# Revit family: GR_Решетка_РАГ-НГ-H_Вытяжка_R21
name_source: partatom
category: Воздухораспределители
units: mm (PartAtom-declared; Revit-internal decimal feet)

## family parameters
Всегда вертикально = Да
Заголовок OmniClass = Diffusers, Registers, and Grilles
На основе рабочей плоскости = Нет
Номер OmniClass = 23.75.70.21.27.11
Общий = Нет
При загрузке вырезать с полостями = Да
Размер круглого соединителя = Использовать диаметр
Тип детали = Нормальный
Точка принадлежности помещению = Нет

## types (2) — shared parameters
ADSK_URL страницы изделия = https://grilles.ru
ADSK_Автор = THE GRILLES
ADSK_Версия Revit = 2021
ADSK_Версия семейства = v1
ADSK_Единица измерения = шт.
ADSK_Завод-изготовитель = ООО "ВЕНТРЕШЕТКИКОМ"
ADSK_Код изделия = 002057
ADSK_Количество = 1
ADSK_Наименование = Решетка нерегулируемая вытяжная РАГ-НГ-Н
GR_Материал решетки = Сталь, RAL 9016M, белый
URL = https://grilles.ru
Изготовитель = ООО "ВЕНТРЕШЕТКИКОМ"
zero-valued in all types: Отметка по умолчанию

## per-type parameters (varying)
| type | Марка_Тип | Описание | РАГ-НГ-1-H | РАГ-НГ-2-H |
| РАГ-НГ-1-Н | РАГ-НГ-1-H_Mark | Однорядная нерегулируемая накладная решетка РАГ-НГ-Н используются в приточно-вытяжной вентиляции и системах
кондиционирования воздуха и предназначены для установки в стены,
воздуховоды и потолочные проемы. Конструктивным отличием является
накладной тип исполнения, ее рамка сделана без внешнего фланца. Решетка
РАГ-НГ-Н накладывается на проем, либо полностью утапливается в проеме.
Решетка имеет рамку и горизонтально расположенные каплеобразные
жалюзи, которые могут быть зафиксированы под углом 30˚, 45˚ и 90˚
специальной пластиной с вырезами, что исключает провисание жалюзи и
повышает эстетический вид изделия. Жалюзи возможно расположить по
типу 1 во внутреннюю сторону (РАГ-НГ-Н-1) и по типу 2 во внешнюю сторону
(РАГ-НГ-Н-2). | Да | Нет |
| РАГ-НГ-2-Н | РАГ-НГ-2-H_Mark | Однорядная нерегулируемая решетка РАГ-НГ используется в
приточно-вытяжной вентиляции и системах кондиционирования воздуха и
предназначена для установки в стены, воздуховоды и потолочные проемы.
Решетка имеет рамку и горизонтально расположенные каплеобразные
жалюзи, которые могут быть зафиксированы под углом 30˚, 45˚ и 90˚
специальной пластиной с вырезами, что исключает провисание жалюзи и
повышает эстетический вид изделия. Жалюзи возможно расположить по типу
1 во внутреннюю сторону (РАГ-НГ-1) и по типу 2 во внешнюю сторону (РАГ-НГ-2) | Нет | Да |
